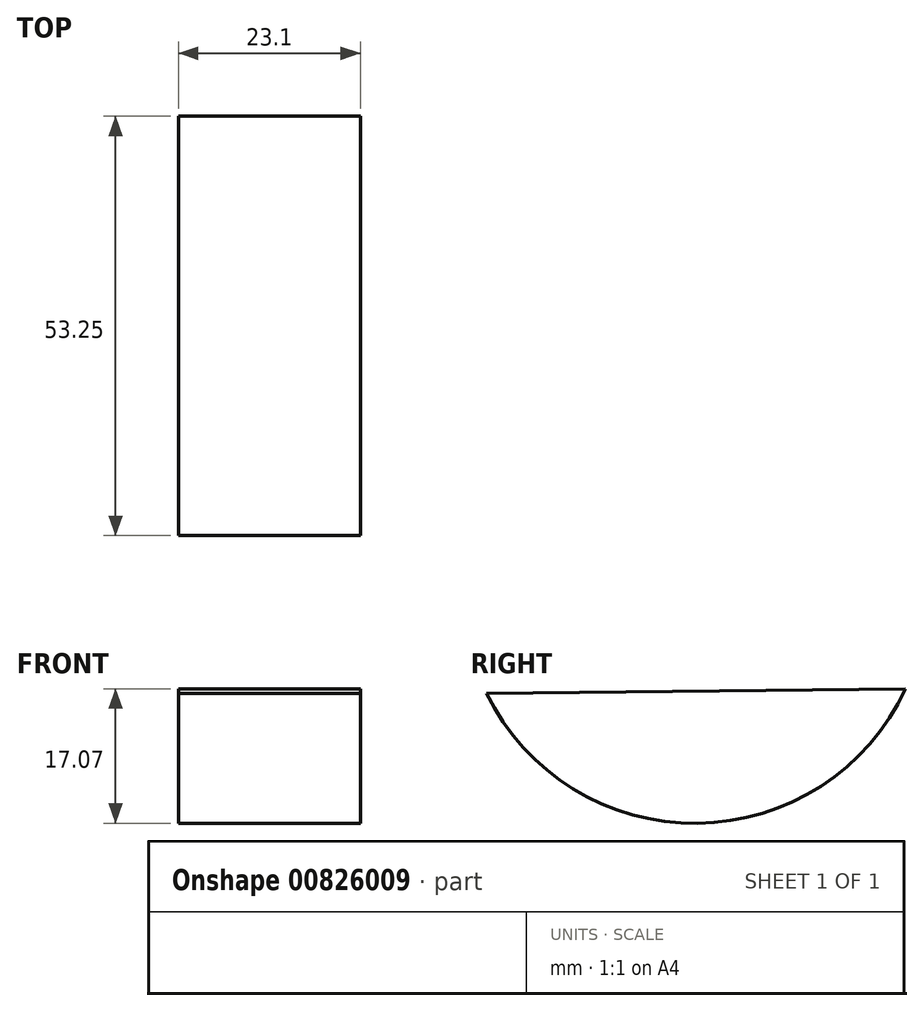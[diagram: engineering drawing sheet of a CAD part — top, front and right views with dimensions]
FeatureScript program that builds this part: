
annotation { "Feature Type Name" : "Feature", "Feature Type Description" : "" }
export const myFeature = defineFeature(function(context is Context, id is Id, definition is map)
    precondition{}
    {
        {
            var Q0;
            Q0=qCreatedBy(makeId("Right.planeOp"),FACE);
            var sketch = newSketch(context, id + "F0", { "sketchPlane" : qUnion([Q0])});
            skArc(sketch, "E0", {"start": v(-62.46, 48.01) * mm, "mid": v(-35.66, 31.5) * mm, "end": v(-9.2, 48.58) * mm});
            skLineSegment(sketch, "E1", {"start": v(-62.46, 48.01) * mm, "end": v(-9.2, 48.58) * mm});
            skSolve(sketch);
        }
        {
            var Q0;
            Q0=makeQuery(id+"F0.imprint","IMPRINT",FACE,{"disambiguationData":[TD([[makeQuery(id+"F0.imprint","IMPRINT",EDGE,{"derivedFrom":sQuery(id+"F0.wireOp",EDGE,"E0")}),1.0]])]});
            extrude(context, id + "F1", {"entities" : qUnion([Q0]), "depth" : 23.1 * mm, "offsetDistance" : 25 * mm});
        }
    });
